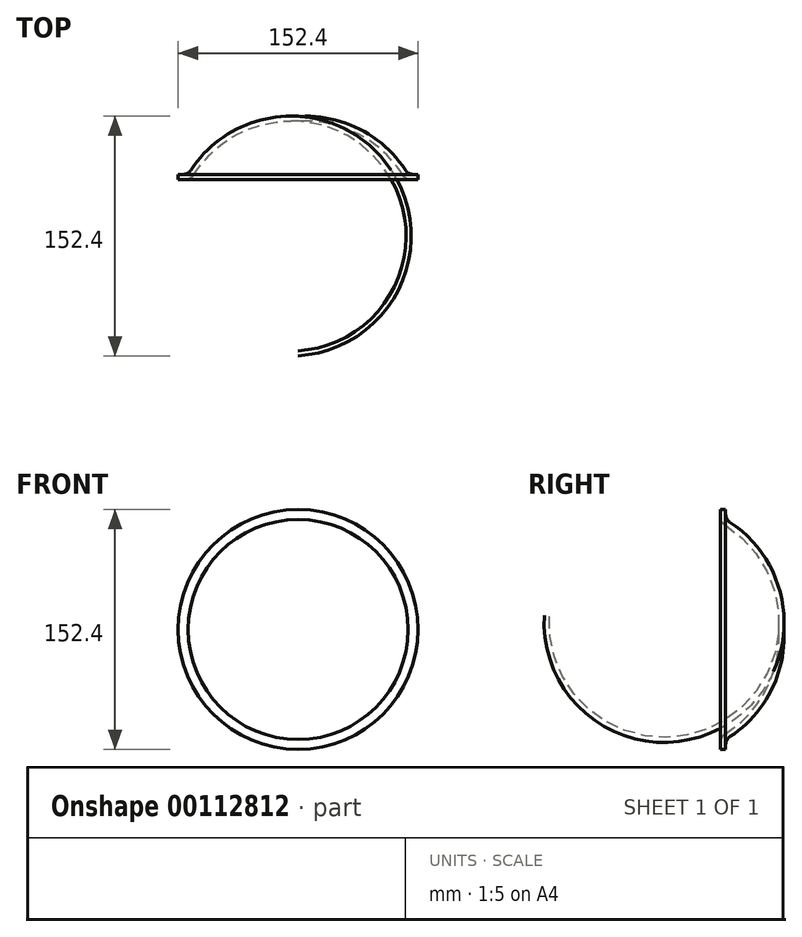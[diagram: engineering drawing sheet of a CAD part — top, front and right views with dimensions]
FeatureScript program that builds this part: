
annotation { "Feature Type Name" : "Feature", "Feature Type Description" : "" }
export const myFeature = defineFeature(function(context is Context, id is Id, definition is map)
    precondition{}
    {
        {
            var Q0;
            Q0=qCreatedBy(makeId("Top.planeOp"),FACE);
            var sketch = newSketch(context, id + "F0", { "sketchPlane" : qUnion([Q0])});
            skArc(sketch, "E0", {"start": v(68.06, 2.85) * mm, "mid": v(38.59, 29) * mm, "end": v(0, 36.94) * mm});
            skLineSegment(sketch, "E1", {"start": v(73.36, 0) * mm, "end": v(76.2, 0) * mm});
            skLineSegment(sketch, "E2", {"start": v(76.2, 0) * mm, "end": v(76.2, -3.17) * mm});
            skLineSegment(sketch, "E3", {"start": v(76.2, -3.17) * mm, "end": v(69.85, -3.17) * mm});
            skArc(sketch, "E4.0", {"start": v(66.3, -0.3) * mm, "mid": v(37.82, 25.83) * mm, "end": v(0, 33.76) * mm});
            skLineSegment(sketch, "E5", {"start": v(68.55, -2.44) * mm, "end": v(69.85, -3.17) * mm});
            skPoint(sketch, "E6.visualSharp", {"position": v(67.13, -1.63) * mm});
            skArc(sketch, "E6.filletArc", {"start": v(66.3, -0.3) * mm, "mid": v(67.3, -1.5) * mm, "end": v(68.55, -2.44) * mm});
            skPoint(sketch, "E7.visualSharp", {"position": v(69.85, 0) * mm});
            skArc(sketch, "E7.filletArc", {"start": v(68.06, 2.85) * mm, "mid": v(70.35, 0.76) * mm, "end": v(73.36, 0) * mm});
            skLineSegment(sketch, "E8", {"start": v(0, 36.94) * mm, "end": v(0, 33.76) * mm});
            skSolve(sketch);
        }
        {
            var Q0;
            Q0=qCreatedBy(makeId("Front.planeOp"),FACE);
            var sketch = newSketch(context, id + "F1", { "sketchPlane" : qUnion([Q0])});
            skCircle(sketch, "E9", {"center": v(0, 0) * mm, "radius": 41.67 * mm});
            skSolve(sketch);
        }
        {
            var Q0;
            Q0=makeQuery(id+"F0.imprint","IMPRINT",FACE,{"disambiguationData":[TD([[makeQuery(id+"F0.imprint","IMPRINT",EDGE,{"derivedFrom":sQuery(id+"F0.wireOp",EDGE,"E0")}),1.0]])]});
            var Q1;
            Q1=sQuery(id+"F1.wireOp",EDGE,"E9");
            revolve(context, id + "F2", {"entities" : qUnion([Q0]), "axis" : qUnion([Q1]), "revolveType" : RevolveType.FULL});
        }
    });
